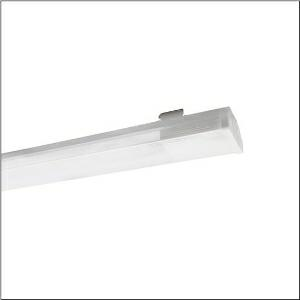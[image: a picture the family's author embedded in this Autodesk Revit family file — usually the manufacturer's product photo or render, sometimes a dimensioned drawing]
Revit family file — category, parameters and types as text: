
# Revit family: modario_31_gen_2_53bm812du4gxc2_8020
name_source: partatom
category: Lighting Fixtures
units: mm (PartAtom-declared; Revit-internal decimal feet)

## family parameters
Cut with Voids When Loaded = No
Host = Face
Light Source = No
Part Type = Normal
Room Calculation Point = No
Round Connector Dimension = Use Diameter
Shared = No

## types (1)
- --- (1 x LED, 16290 lm, 92.1 W, 4000K)
    Apparent Load = 92 VA
    CIE Flux Codes = 47 80 95 93 100
    Color Rendering = 80
    Color Temperature = 4000K
    Default Elevation = 1800 mm
    Description = Modario 31 Gen.2, luminaire insert, of sheet steel, coil coated, white, length: 2.392mm, width: 81mm, height: 82mm, 8x system unit, system units: 299mm, LED rated luminous flux: 16.290lm, light colour: 840, SDCM (Standard Deviation of Colour Matching)MacAdam ≤ 3 SDCM (initial), control gear: DALI 2, control gear: ECG DALI, with plug, 5-pole, with phase selection, mains connection: 220..240V, AC, 50/60Hz, rated input power: 92W, through-wiring accessed according to module size, primary optical cover: cover, of PMMA, light emission: direct distribution, primary light characteristic: symmetric, protection rating (complete): IP20, protection rating (LED compartment): IP50, insulation class (complete): insulation class I (protective earthing), certification: CE, ENEC, VDE, UKCA, impact resistance: IK03, permissible ambient temperature for indoor applications: -25..+40°C, corresponds to IFS (International Featured Standards) requirements for safety and quality in the food industry, reducing of maximum allowable ambient temperature of 5°C with ceiling mounting, IP40 when using the optional accessory 5TP9018, packaging unit: 1 piece
    Height = 92 mm
    Lamp = 1 x LED
    Lamp Light Flux = 16290 lm
    Lamp Power = 92.1 W
    Lamp count = 1
    Length = 2392 mm
    Luminous efficacy = 177 lm/W
    Manufacturer = Siteco
    ModVariant = No
    Model = 53BM812DU4GXC2
    Mounting Place = Ceiling
    Mounting Type = Pendant
    Number of Poles = 1
    OnlyDefault = Yes
    Power Factor = 1
    Product Name = Modario 31 Gen.2
    Product group = luminaire insert | ceiling pendant
    ProductGroupID = 901
    Protection Class = Protection class I
    Protection Degree = IP 20
    RLX_Detail_Level = 1
    RLX_Emergency_Light_Flux = 0 lm
    RLX_Emergency_Type = 0
    RLX_Emergency_Type_DB = No
    RlxData = <blob elided: 38325 chars, md5=4741a91b>
    Socket = socket
    Standby Power = 0 W
    System Light Flux = 16290 lm
    System Power = 92 W
    Type Comments = factory setting: luminous flux: 100 % | dim-lin: 254 | 418 mA
    Type Image = l_1341883.jpg
    URL = http://relux.com
    VarID = @adj_050977
    Voltage = 0 V
    Weight = 0.00 kg
    Width = 81 mm

## geometry (parser evidence)
native form markers: Blend x4, Sweep x12
no freeform markers — native parametric forms only
